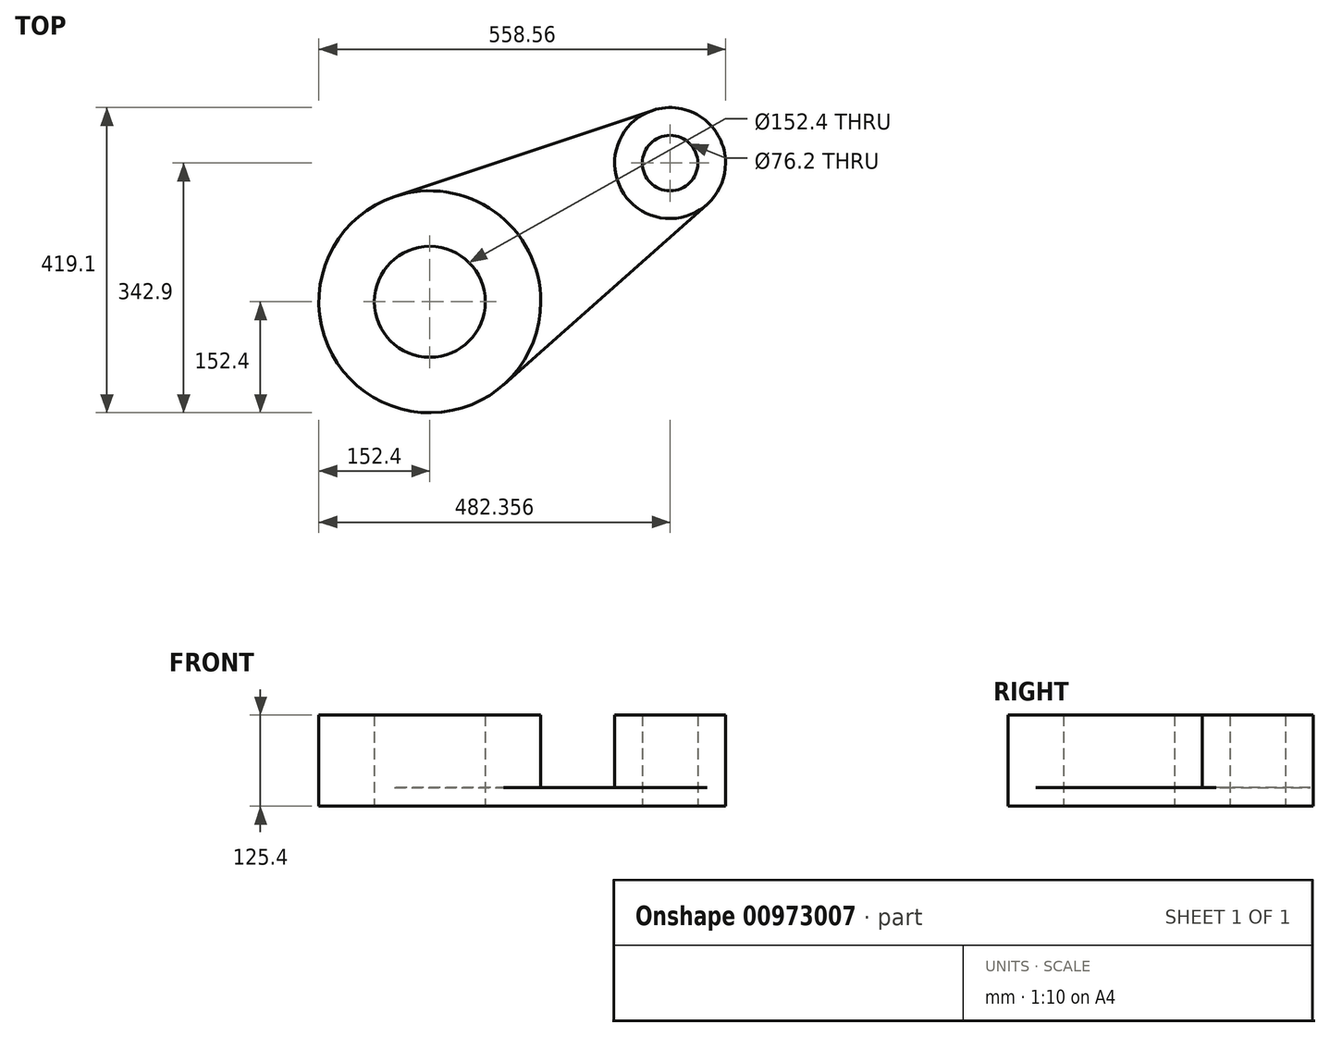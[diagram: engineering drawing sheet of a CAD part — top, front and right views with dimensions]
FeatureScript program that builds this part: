
annotation { "Feature Type Name" : "Feature", "Feature Type Description" : "" }
export const myFeature = defineFeature(function(context is Context, id is Id, definition is map)
    precondition{}
    {
        {
            var Q0;
            Q0=qCreatedBy(makeId("Top.planeOp"),FACE);
            var sketch = newSketch(context, id + "F0", { "sketchPlane" : qUnion([Q0])});
            skCircle(sketch, "E0", {"center": v(0, 0) * mm, "radius": 76.2 * mm});
            skCircle(sketch, "E1", {"center": v(0, 0) * mm, "radius": 152.4 * mm});
            skCircle(sketch, "E2", {"center": v(329.96, 190.5) * mm, "radius": 38.1 * mm});
            skCircle(sketch, "E3", {"center": v(329.96, 190.5) * mm, "radius": 76.2 * mm});
            skLineSegment(sketch, "E4", {"start": v(0, 0) * mm, "end": v(329.96, 190.5) * mm, "construction": true});
            skLineSegment(sketch, "E5", {"start": v(0, 0) * mm, "end": v(415.97, 0) * mm, "construction": true});
            skLineSegment(sketch, "E6", {"start": v(380.48, 133.46) * mm, "end": v(101.06, -114.08) * mm});
            skLineSegment(sketch, "E7", {"start": v(-48.26, 144.56) * mm, "end": v(305.82, 262.78) * mm});
            skSolve(sketch);
        }
        {
            var Q0;
            Q0 = qSketchRegion(id + "F0", true);
            extrude(context, id + "F1", {"entities" : qUnion([Q0]), "depth" : 25.4 * mm, "offsetDistance" : 25.4 * mm});
        }
        {
            var Q0;
            Q0=makeQuery(id+"F1.opExtrude","CAP_FACE",FACE,{"disambiguationData":[OSD([sQuery(id+"F0.wireOp",EDGE,"E0"),sQuery(id+"F0.wireOp",EDGE,"E1"),sQuery(id+"F0.wireOp",EDGE,"E2"),sQuery(id+"F0.wireOp",EDGE,"E3"),sQuery(id+"F0.wireOp",EDGE,"E6"),sQuery(id+"F0.wireOp",EDGE,"E7")])],"isStart":false});
            var sketch = newSketch(context, id + "F2", { "sketchPlane" : qUnion([Q0])});
            skCircle(sketch, "E8.0", {"center": v(0, 0) * mm, "radius": 76.2 * mm});
            skCircle(sketch, "E9.0", {"center": v(0, 0) * mm, "radius": 152.4 * mm});
            skSolve(sketch);
        }
        {
            var Q0;
            Q0 = qSketchRegion(id + "F2", true);
            extrude(context, id + "F3", {"entities" : qUnion([Q0]), "operationType" : NewBodyOperationType.ADD, "depth" : 100 * mm, "offsetDistance" : 25 * mm});
        }
        {
            var Q0;
            Q0=makeQuery(id+"F1.opExtrude","CAP_FACE",FACE,{"disambiguationData":[OSD([sQuery(id+"F0.wireOp",EDGE,"E0"),sQuery(id+"F0.wireOp",EDGE,"E1"),sQuery(id+"F0.wireOp",EDGE,"E2"),sQuery(id+"F0.wireOp",EDGE,"E3"),sQuery(id+"F0.wireOp",EDGE,"E6"),sQuery(id+"F0.wireOp",EDGE,"E7")])],"isStart":false});
            var sketch = newSketch(context, id + "F4", { "sketchPlane" : qUnion([Q0])});
            skCircle(sketch, "E10.0", {"center": v(329.96, 190.5) * mm, "radius": 38.1 * mm});
            skCircle(sketch, "E11.0", {"center": v(329.96, 190.5) * mm, "radius": 76.2 * mm});
            skSolve(sketch);
        }
        {
            var Q0;
            Q0 = qSketchRegion(id + "F4", true);
            var Q1;
            Q1=makeQuery(id+"F3.opExtrude","CAP_FACE",FACE,{"disambiguationData":[OSD([sQuery(id+"F2.wireOp",EDGE,"E8.0"),sQuery(id+"F2.wireOp",EDGE,"E9.0")])],"isStart":false});
            extrude(context, id + "F5", {"entities" : qUnion([Q0]), "operationType" : NewBodyOperationType.ADD, "endBound" : BoundingType.UP_TO_SURFACE, "depth" : 25 * mm, "endBoundEntityFace" : qUnion([Q1]), "offsetDistance" : 25 * mm});
        }
    });
